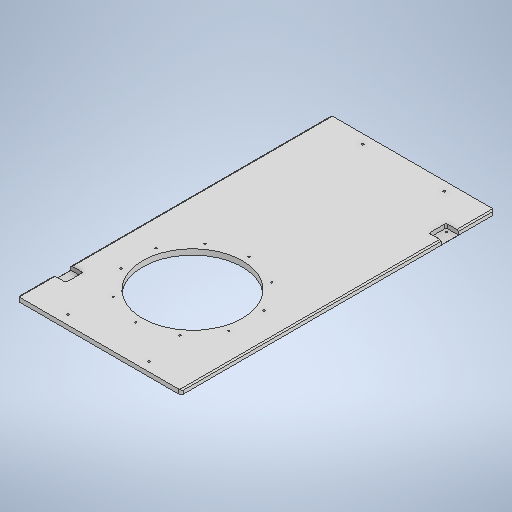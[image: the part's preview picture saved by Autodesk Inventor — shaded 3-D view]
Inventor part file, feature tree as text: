
AUTODESK INVENTOR PART (.ipt)
format: ipt  version: 2025 (Build 290162000, 162)  size: 414,720 bytes
history: native  units: in
note: dims shown in document units (in); Inventor stores cm internally (conversion verified against a paired STEP export)
features: sketch x9, extrude x5, hole x3, chamfer x3, plane x2, fillet x2, pattern_circular x1
ambient origin geometry x8: Origin, YZ Plane, XZ Plane, XY Plane, X Axis, Y Axis, Z Axis, Center Point
bodies: Solid1 (feature_tree)
feature tree (25):
  extrude  "Base Cover"  Depth=27.1654in
  sketch  "Sketch2"  dims[d2=0.4724in d3=0.0in d4=8.0709in]
  extrude  "Cylinder Hole"  Depth=0.4724in
  plane  "Work Plane1"
  hole  "Handle Holes"  [1 undecoded]
  sketch  "Sketch7"  dims[d8=10.6299in d50=5.9055in d55=7.0625in]
  plane  "Work Plane2"
  hole  "Cylinder Mount Holes"  [1 undecoded]
  sketch  "Sketch9"  dims[d57=0.1936in d58=0.1969in d59=0.1575in d60=0.0787in d61=90.0deg d62=0.1969in d63=0.8108in]
  fillet  "Rounded Side Corners"  Radius=7.0625in
  chamfer  "Chamfer1"  Distance=1.063in
  chamfer  "Chamfer2"  Distance=1.063in
  extrude  "Magnet Seats"  Depth=0.3937in
  hole  "Magnet Holes"  [1 undecoded]
  chamfer  "Chamfer5"  Distance=3.1102in
  fillet  "Rounded Bottom Corners"  Radius=3.1102in
  extrude  "Extrusion14"  Depth=0.3937in
  extrude  "Extrusion15"  Depth=0.3937in TaperAngle=45.0deg
  pattern_circular  "Circular Pattern1"  Angle=45.0deg  [1 undecoded]
  sketch  "Sketch1"  dims[d0=14.1732in d1=27.1654in]
  sketch  "Sketch6"  dims[d5=8.6614in d6=0.0in d7=0.0in]
  sketch  "Sketch8"  dims[d56=25.5906in]
  sketch  "Sketch11"  dims[d64=10.3543in]
  sketch  "Sketch18"  dims[d65=10.6299in]
  sketch  "Sketch19"  dims[d68=9.8425in d74=0.1628in d75=0.3937in d76=0.1575in d77=0.0787in d78=90.0deg d79=0.3937in d80=0.8108in d82=1.063in d83=1.063in d84=1.4961in d85=1.4961in d86=3.1102in d87=3.1102in d88=0.1969in d89=0.0984in d90=0.0787in d91=45.0deg d92=0.0984in d93=0.0787in d94=45.0deg d95=0.1181in d96=0.1181in d97=0.3543in d98=0.0in d109=0.748in d110=0.315in d111=0.8661in d112=0.748in d113=0.1299in d114=0.1299in d115=0.1299in d116=0.1299in d118=0.315in d119=0.8661in d120=0.748in d121=0.748in d122=0.1276in d123=0.315in d124=0.1575in d125=0.0787in d126=90.0deg d127=0.315in d128=0.8108in d129=0.0138in d130=0.0787in d131=45.0deg d230=0.2756in d243=0.1378in d244=0.0787in d245=0.3848in d246=0.0in d247=0.1378in d248=0.0787in d249=0.3937in d250=0.0in d278=0.1575in d279=3.937in d280=360.0deg d26=0.0394in d27=0.0394in d28=0.0394in d29=0.0059in d30=0.0098in d31=0.0148in d32=0.5635in d33=0.0295in d34=0.8108in d35=0.0025in d36=0.0295in d37=0.0148in d66=0.0197in d67=0.0344in d251=0.0394in d252=0.0394in d253=0.0394in d254=0.0059in d255=0.0098in d256=0.0148in d257=0.5635in d258=0.0295in d259=0.8108in d260=0.0025in d261=0.0295in d262=0.0148in d263=0.0394in d264=0.0394in d265=0.0059in d266=0.0098in d267=0.0148in d268=0.5635in d269=0.0295in d270=0.8108in d271=0.0025in d272=0.0295in d273=0.0148in]
note: 4 required parameter values undecoded (feature->parameter linkage not recoverable at this tier; creation-order binding heuristic only, values carry confidence <= 0.55)
